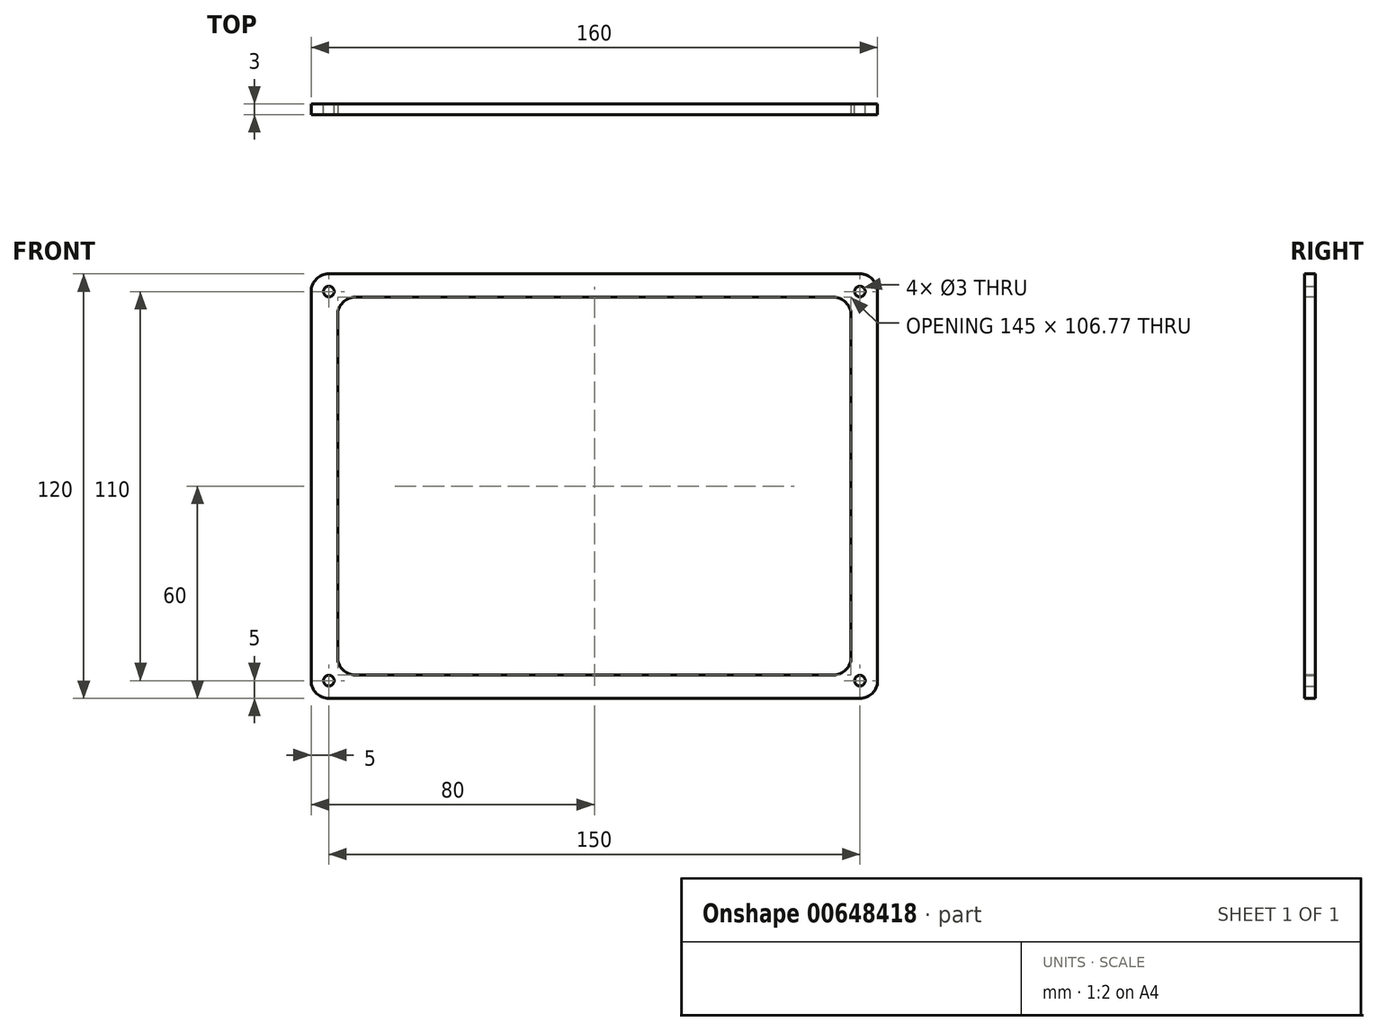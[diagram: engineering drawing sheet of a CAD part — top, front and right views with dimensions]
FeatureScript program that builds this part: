
annotation { "Feature Type Name" : "Feature", "Feature Type Description" : "" }
export const myFeature = defineFeature(function(context is Context, id is Id, definition is map)
    precondition{}
    {
        {
            var Q0;
            Q0=qCreatedBy(makeId("Front.planeOp"),FACE);
            var sketch = newSketch(context, id + "F0", { "sketchPlane" : qUnion([Q0])});
            skLineSegment(sketch, "E0.bottom", {"start": v(75, -60) * mm, "end": v(-75, -60) * mm});
            skLineSegment(sketch, "E0.top", {"start": v(75, 60) * mm, "end": v(-75, 60) * mm});
            skLineSegment(sketch, "E0.left", {"start": v(80, -55) * mm, "end": v(80, 55) * mm});
            skLineSegment(sketch, "E0.right", {"start": v(-80, -55) * mm, "end": v(-80, 55) * mm});
            skPoint(sketch, "E0.middle", {"position": v(0, 0) * mm});
            skPoint(sketch, "E1.visualSharp", {"position": v(-80, 60) * mm});
            skArc(sketch, "E1.filletArc", {"start": v(-75, 60) * mm, "mid": v(-78.54, 58.54) * mm, "end": v(-80, 55) * mm});
            skPoint(sketch, "E2.visualSharp", {"position": v(80, 60) * mm});
            skArc(sketch, "E2.filletArc", {"start": v(80, 55) * mm, "mid": v(78.54, 58.54) * mm, "end": v(75, 60) * mm});
            skPoint(sketch, "E3.visualSharp", {"position": v(80, -60) * mm});
            skArc(sketch, "E3.filletArc", {"start": v(75, -60) * mm, "mid": v(78.54, -58.54) * mm, "end": v(80, -55) * mm});
            skPoint(sketch, "E4.visualSharp", {"position": v(-80, -60) * mm});
            skArc(sketch, "E4.filletArc", {"start": v(-80, -55) * mm, "mid": v(-78.54, -58.54) * mm, "end": v(-75, -60) * mm});
            skSolve(sketch);
        }
        {
            var Q0;
            Q0=makeQuery(id+"F0.imprint","IMPRINT",FACE,{"disambiguationData":[TD([[makeQuery(id+"F0.imprint","IMPRINT",EDGE,{"derivedFrom":sQuery(id+"F0.wireOp",EDGE,"E0.bottom")}),-1.0]])]});
            extrude(context, id + "F1", {"entities" : qUnion([Q0]), "depth" : 3 * mm, "offsetDistance" : 25 * mm});
        }
        {
            var Q0;
            Q0=qCreatedBy(makeId("Front.planeOp"),FACE);
            var sketch = newSketch(context, id + "F2", { "sketchPlane" : qUnion([Q0])});
            skCircle(sketch, "E5", {"center": v(-75, 55) * mm, "radius": 1.5 * mm});
            skCircle(sketch, "E6", {"center": v(75, 55) * mm, "radius": 1.5 * mm});
            skCircle(sketch, "E7", {"center": v(75, -55) * mm, "radius": 1.5 * mm});
            skCircle(sketch, "E8", {"center": v(-75, -55) * mm, "radius": 1.5 * mm});
            skSolve(sketch);
        }
        {
            var Q0;
            Q0=qSketchRegion(id+"F2",true);
            extrude(context, id + "F3", {"entities" : qUnion([Q0]), "operationType" : NewBodyOperationType.REMOVE, "depth" : 25 * mm, "offsetDistance" : 25 * mm});
        }
        {
            var Q0;
            Q0=makeQuery(id+"F1.opExtrude","CAP_FACE",FACE,{"disambiguationData":[OSD([sQuery(id+"F0.wireOp",EDGE,"E0.bottom"),sQuery(id+"F0.wireOp",EDGE,"E0.top"),sQuery(id+"F0.wireOp",EDGE,"E0.left"),sQuery(id+"F0.wireOp",EDGE,"E0.right"),sQuery(id+"F0.wireOp",EDGE,"E1.filletArc"),sQuery(id+"F0.wireOp",EDGE,"E2.filletArc"),sQuery(id+"F0.wireOp",EDGE,"E3.filletArc"),sQuery(id+"F0.wireOp",EDGE,"E4.filletArc")])],"isStart":false});
            var sketch = newSketch(context, id + "F4", { "sketchPlane" : qUnion([Q0])});
            skLineSegment(sketch, "E9.bottom", {"start": v(67.5, 53.39) * mm, "end": v(-67.5, 53.39) * mm});
            skLineSegment(sketch, "E9.top", {"start": v(67.5, -53.39) * mm, "end": v(-67.5, -53.39) * mm});
            skLineSegment(sketch, "E9.left", {"start": v(72.5, 48.39) * mm, "end": v(72.5, -48.39) * mm});
            skLineSegment(sketch, "E9.right", {"start": v(-72.5, 48.39) * mm, "end": v(-72.5, -48.39) * mm});
            skPoint(sketch, "E9.middle", {"position": v(0, 0) * mm});
            skPoint(sketch, "E10.visualSharp", {"position": v(-72.5, 53.39) * mm});
            skArc(sketch, "E10.filletArc", {"start": v(-67.5, 53.39) * mm, "mid": v(-71.04, 51.92) * mm, "end": v(-72.5, 48.39) * mm});
            skPoint(sketch, "E11.visualSharp", {"position": v(72.5, 53.39) * mm});
            skArc(sketch, "E11.filletArc", {"start": v(72.5, 48.39) * mm, "mid": v(71.04, 51.92) * mm, "end": v(67.5, 53.39) * mm});
            skPoint(sketch, "E12.visualSharp", {"position": v(72.5, -53.39) * mm});
            skArc(sketch, "E12.filletArc", {"start": v(67.5, -53.39) * mm, "mid": v(71.04, -51.92) * mm, "end": v(72.5, -48.39) * mm});
            skPoint(sketch, "E13.visualSharp", {"position": v(-72.5, -53.39) * mm});
            skArc(sketch, "E13.filletArc", {"start": v(-72.5, -48.39) * mm, "mid": v(-71.04, -51.92) * mm, "end": v(-67.5, -53.39) * mm});
            skSolve(sketch);
        }
        {
            var Q0;
            Q0=makeQuery(id+"F4.imprint","IMPRINT",FACE,{"disambiguationData":[TD([[makeQuery(id+"F4.imprint","IMPRINT",EDGE,{"derivedFrom":sQuery(id+"F4.wireOp",EDGE,"E9.bottom")}),1.0]])]});
            extrude(context, id + "F5", {"entities" : qUnion([Q0]), "operationType" : NewBodyOperationType.REMOVE, "oppositeDirection" : true, "depth" : 3 * mm, "offsetDistance" : 25 * mm});
        }
    });
